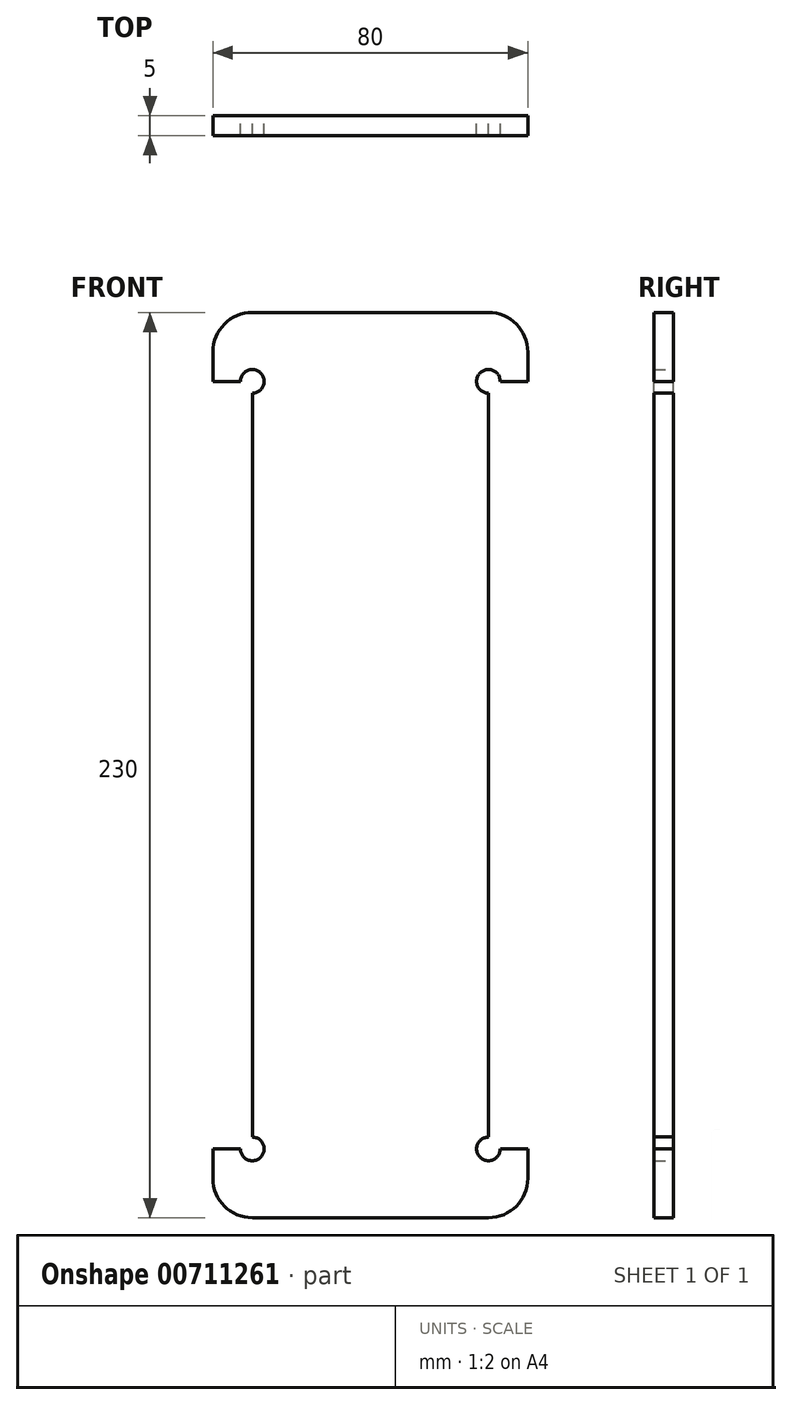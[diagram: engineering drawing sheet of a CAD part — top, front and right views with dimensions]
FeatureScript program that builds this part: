
annotation { "Feature Type Name" : "Feature", "Feature Type Description" : "" }
export const myFeature = defineFeature(function(context is Context, id is Id, definition is map)
    precondition{}
    {
        {
            var Q0;
            Q0=qCreatedBy(makeId("Front.planeOp"),FACE);
            var sketch = newSketch(context, id + "F0", { "sketchPlane" : qUnion([Q0])});
            skLineSegment(sketch, "E0.bottom", {"start": v(30, 115) * mm, "end": v(-30, 115) * mm});
            skLineSegment(sketch, "E0.top", {"start": v(30, -115) * mm, "end": v(-30, -115) * mm});
            skLineSegment(sketch, "E0.left", {"start": v(40, 105) * mm, "end": v(40, 97.5) * mm});
            skLineSegment(sketch, "E0.right", {"start": v(-40, 105) * mm, "end": v(-40, 97.5) * mm});
            skPoint(sketch, "E0.middle", {"position": v(0, 0) * mm});
            skPoint(sketch, "E1.visualSharp", {"position": v(-40, 115) * mm});
            skArc(sketch, "E1.filletArc", {"start": v(-30, 115) * mm, "mid": v(-37.07, 112.07) * mm, "end": v(-40, 105) * mm});
            skPoint(sketch, "E2.visualSharp", {"position": v(40, 115) * mm});
            skArc(sketch, "E2.filletArc", {"start": v(40, 105) * mm, "mid": v(37.07, 112.07) * mm, "end": v(30, 115) * mm});
            skPoint(sketch, "E3.visualSharp", {"position": v(-40, -115) * mm});
            skArc(sketch, "E3.filletArc", {"start": v(-40, -105) * mm, "mid": v(-37.07, -112.07) * mm, "end": v(-30, -115) * mm});
            skPoint(sketch, "E4.visualSharp", {"position": v(40, -115) * mm});
            skArc(sketch, "E4.filletArc", {"start": v(30, -115) * mm, "mid": v(37.07, -112.07) * mm, "end": v(40, -105) * mm});
            skLineSegment(sketch, "E5.0", {"start": v(-30, 94.5) * mm, "end": v(-30, -94.5) * mm});
            skLineSegment(sketch, "E6", {"start": v(-33, 97.5) * mm, "end": v(-40, 97.5) * mm});
            skLineSegment(sketch, "E7", {"start": v(-33, -97.5) * mm, "end": v(-40, -97.5) * mm});
            skLineSegment(sketch, "E8.trimOffspring", {"start": v(-40, -97.5) * mm, "end": v(-40, -105) * mm});
            skArc(sketch, "E9", {"start": v(-30, 94.5) * mm, "mid": v(-27.88, 99.62) * mm, "end": v(-33, 97.5) * mm});
            skArc(sketch, "E10", {"start": v(-33, -97.5) * mm, "mid": v(-27.88, -99.62) * mm, "end": v(-30, -94.5) * mm});
            skArc(sketch, "E11.MirrorCS", {"start": v(30, 94.5) * mm, "mid": v(27.88, 99.62) * mm, "end": v(33, 97.5) * mm});
            skLineSegment(sketch, "E12.MirrorCS", {"start": v(33, 97.5) * mm, "end": v(40, 97.5) * mm});
            skLineSegment(sketch, "E13.MirrorCS", {"start": v(33, -97.5) * mm, "end": v(40, -97.5) * mm});
            skArc(sketch, "E14.MirrorCS", {"start": v(33, -97.5) * mm, "mid": v(27.88, -99.62) * mm, "end": v(30, -94.5) * mm});
            skLineSegment(sketch, "E15.MirrorCS", {"start": v(40, -97.5) * mm, "end": v(40, -105) * mm});
            skLineSegment(sketch, "E16.MirrorCS", {"start": v(30, 94.5) * mm, "end": v(30, -94.5) * mm});
            skSolve(sketch);
        }
        {
            var Q0;
            Q0=makeQuery(id+"F0.imprint","IMPRINT",FACE,{"disambiguationData":[TD([[makeQuery(id+"F0.imprint","IMPRINT",EDGE,{"derivedFrom":sQuery(id+"F0.wireOp",EDGE,"E0.bottom")}),1.0]])]});
            extrude(context, id + "F1", {"entities" : qUnion([Q0]), "depth" : 5 * mm, "offsetDistance" : 25 * mm});
        }
    });
